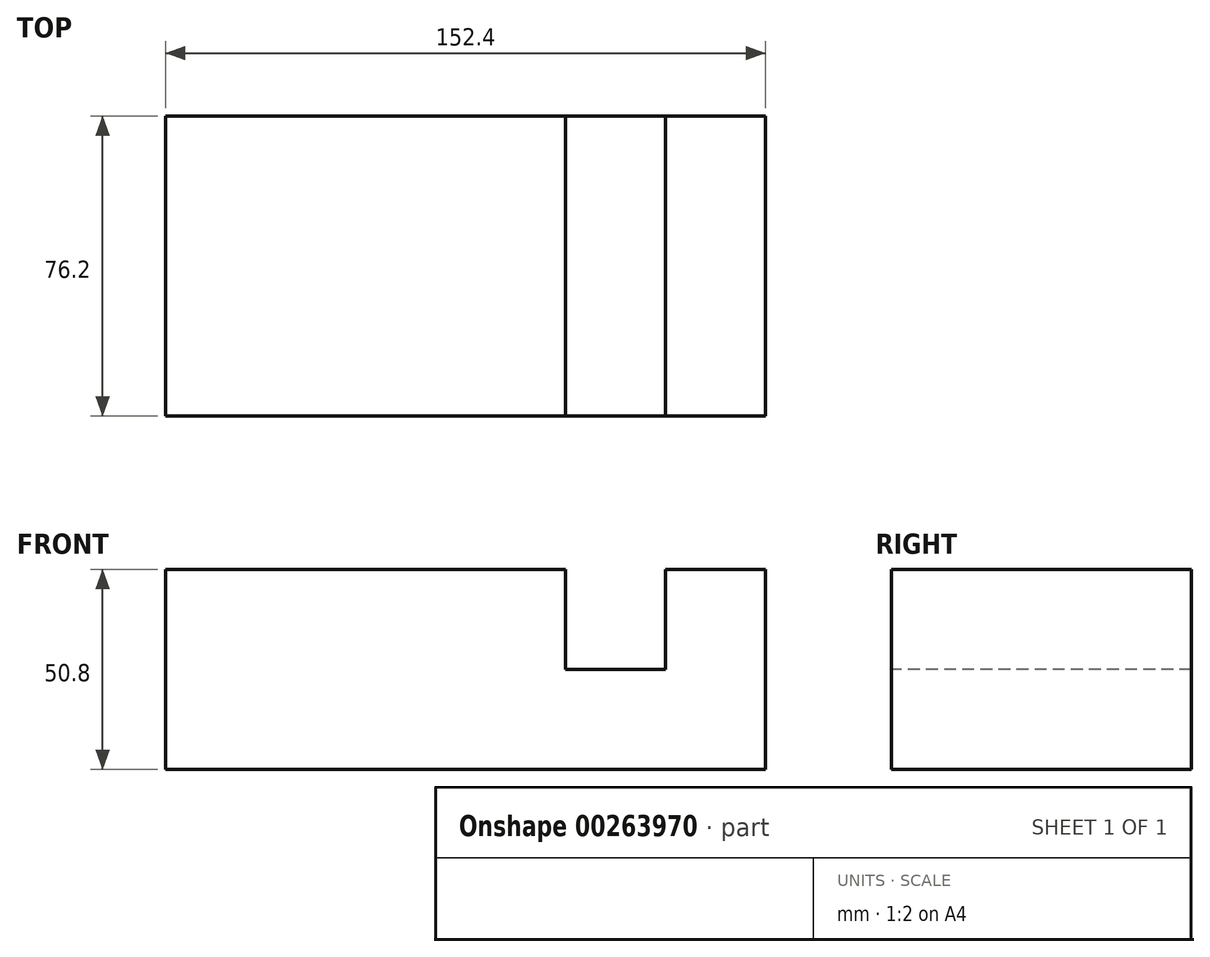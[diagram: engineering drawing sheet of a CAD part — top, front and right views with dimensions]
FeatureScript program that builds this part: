
annotation { "Feature Type Name" : "Feature", "Feature Type Description" : "" }
export const myFeature = defineFeature(function(context is Context, id is Id, definition is map)
    precondition{}
    {
        {
            var Q0;
            Q0=qCreatedBy(makeId("Front.planeOp"),FACE);
            var sketch = newSketch(context, id + "F0", { "sketchPlane" : qUnion([Q0])});
            skLineSegment(sketch, "E0", {"start": v(-76.24, 0) * mm, "end": v(76.16, 0) * mm});
            skLineSegment(sketch, "E1", {"start": v(76.16, 0) * mm, "end": v(76.16, 50.8) * mm});
            skLineSegment(sketch, "E2", {"start": v(76.16, 50.8) * mm, "end": v(50.76, 50.8) * mm});
            skLineSegment(sketch, "E3", {"start": v(50.76, 50.8) * mm, "end": v(50.76, 25.4) * mm});
            skLineSegment(sketch, "E4", {"start": v(50.76, 25.4) * mm, "end": v(25.36, 25.4) * mm});
            skLineSegment(sketch, "E5", {"start": v(25.36, 25.4) * mm, "end": v(25.36, 50.8) * mm});
            skLineSegment(sketch, "E6", {"start": v(25.36, 50.8) * mm, "end": v(-76.24, 50.8) * mm});
            skLineSegment(sketch, "E7", {"start": v(-76.24, 50.8) * mm, "end": v(-76.24, 0) * mm});
            skSolve(sketch);
        }
        {
            var Q0;
            Q0=makeQuery(id+"F0.imprint","IMPRINT",FACE,{"disambiguationData":[TD([[makeQuery(id+"F0.imprint","IMPRINT",EDGE,{"derivedFrom":sQuery(id+"F0.wireOp",EDGE,"E0")}),1.0]])]});
            extrude(context, id + "F1", {"entities" : qUnion([Q0]), "oppositeDirection" : true, "depth" : 76.2 * mm});
        }
    });
